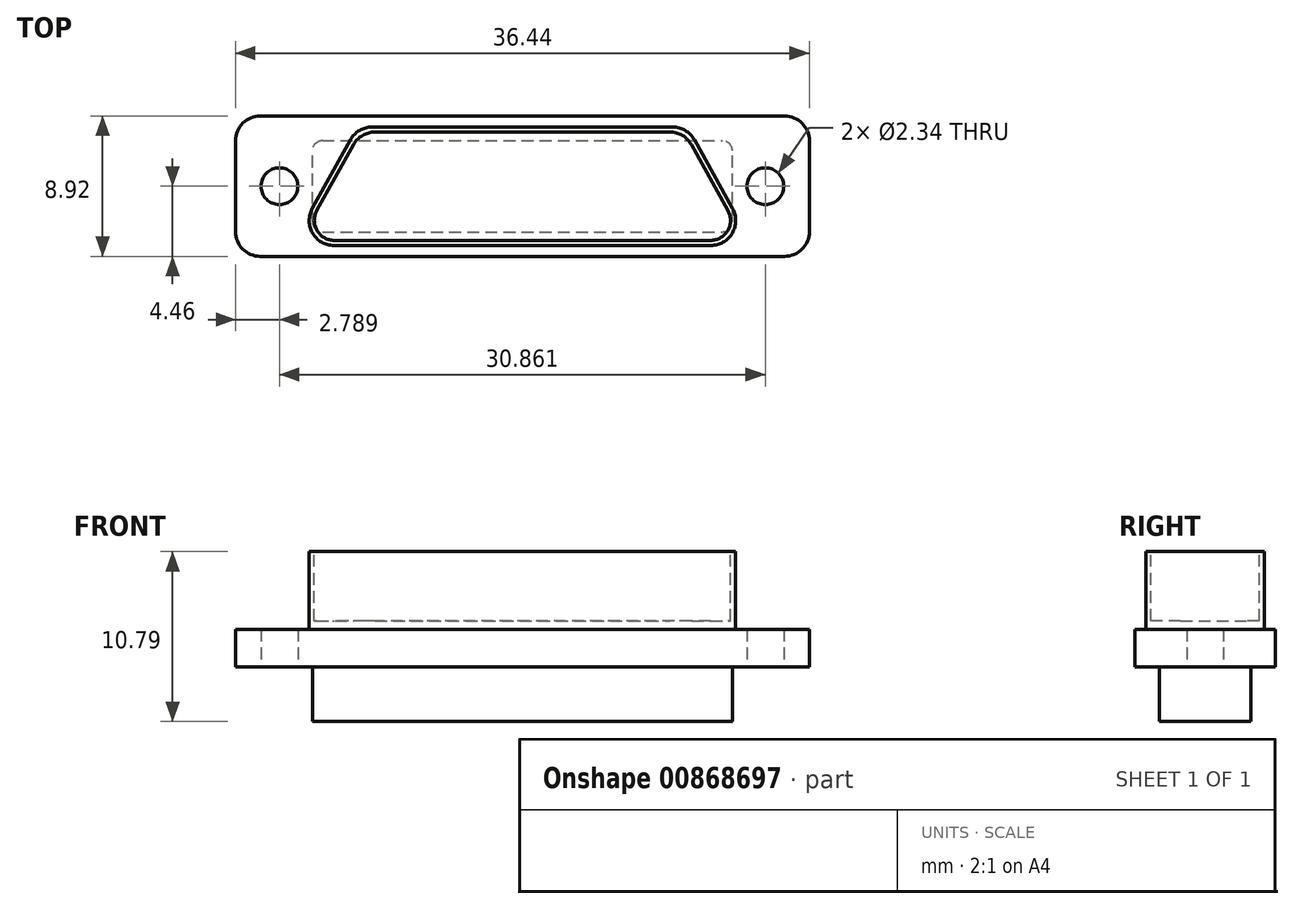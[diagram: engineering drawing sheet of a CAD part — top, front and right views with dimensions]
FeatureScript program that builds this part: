
annotation { "Feature Type Name" : "Feature", "Feature Type Description" : "" }
export const myFeature = defineFeature(function(context is Context, id is Id, definition is map)
    precondition{}
    {
        {
            var Q0;
            Q0=qCreatedBy(makeId("Top.planeOp"),FACE);
            var sketch = newSketch(context, id + "F0", { "sketchPlane" : qUnion([Q0])});
            skLineSegment(sketch, "E0.bottom", {"start": v(-16.65, 4.46) * mm, "end": v(16.65, 4.46) * mm});
            skLineSegment(sketch, "E0.top", {"start": v(-16.65, -4.46) * mm, "end": v(16.65, -4.46) * mm});
            skLineSegment(sketch, "E0.left", {"start": v(-18.22, 2.88) * mm, "end": v(-18.22, -2.88) * mm});
            skLineSegment(sketch, "E0.right", {"start": v(18.22, 2.88) * mm, "end": v(18.22, -2.88) * mm});
            skPoint(sketch, "E0.middle", {"position": v(0, 0) * mm});
            skCircle(sketch, "E1", {"center": v(-15.43, 0) * mm, "radius": 1.17 * mm});
            skCircle(sketch, "E2", {"center": v(15.43, 0) * mm, "radius": 1.17 * mm});
            skPoint(sketch, "E3.visualSharp", {"position": v(-18.22, -4.46) * mm});
            skArc(sketch, "E3.filletArc", {"start": v(-18.22, -2.88) * mm, "mid": v(-17.76, -4) * mm, "end": v(-16.65, -4.46) * mm});
            skPoint(sketch, "E4.visualSharp", {"position": v(-18.22, 4.46) * mm});
            skArc(sketch, "E4.filletArc", {"start": v(-16.65, 4.46) * mm, "mid": v(-17.76, 4) * mm, "end": v(-18.22, 2.88) * mm});
            skPoint(sketch, "E5.visualSharp", {"position": v(18.22, 4.46) * mm});
            skArc(sketch, "E5.filletArc", {"start": v(18.22, 2.88) * mm, "mid": v(17.76, 4) * mm, "end": v(16.65, 4.46) * mm});
            skPoint(sketch, "E6.visualSharp", {"position": v(18.22, -4.46) * mm});
            skArc(sketch, "E6.filletArc", {"start": v(16.65, -4.46) * mm, "mid": v(17.76, -4) * mm, "end": v(18.22, -2.88) * mm});
            skSolve(sketch);
        }
        {
            var Q0;
            Q0=makeQuery(id+"F0.imprint","IMPRINT",FACE,{"disambiguationData":[TD([[makeQuery(id+"F0.imprint","IMPRINT",EDGE,{"derivedFrom":sQuery(id+"F0.wireOp",EDGE,"E0.bottom")}),-1.0]])]});
            extrude(context, id + "F1", {"entities" : qUnion([Q0]), "endBound" : BoundingType.SYMMETRIC, "depth" : 2.36 * mm, "offsetDistance" : 25.4 * mm});
        }
        {
            var Q0;
            Q0=makeQuery(id+"F1.opExtrude","CAP_FACE",FACE,{"disambiguationData":[OSD([sQuery(id+"F0.wireOp",EDGE,"E0.bottom"),sQuery(id+"F0.wireOp",EDGE,"E0.top"),sQuery(id+"F0.wireOp",EDGE,"E0.left"),sQuery(id+"F0.wireOp",EDGE,"E0.right"),sQuery(id+"F0.wireOp",EDGE,"E1"),sQuery(id+"F0.wireOp",EDGE,"E2"),sQuery(id+"F0.wireOp",EDGE,"E3.filletArc"),sQuery(id+"F0.wireOp",EDGE,"E4.filletArc"),sQuery(id+"F0.wireOp",EDGE,"E5.filletArc"),sQuery(id+"F0.wireOp",EDGE,"E6.filletArc")])],"isStart":false});
            var sketch = newSketch(context, id + "F2", { "sketchPlane" : qUnion([Q0])});
            skPoint(sketch, "E7.middle", {"position": v(0, 0) * mm});
            skLineSegment(sketch, "E8.top", {"start": v(11.97, -3.76) * mm, "end": v(-11.97, -3.76) * mm});
            skLineSegment(sketch, "E9", {"start": v(-9.55, 3.76) * mm, "end": v(9.55, 3.76) * mm});
            skLineSegment(sketch, "E10", {"start": v(-13.35, -1.42) * mm, "end": v(-10.93, 2.95) * mm});
            skLineSegment(sketch, "E11", {"start": v(10.93, 2.95) * mm, "end": v(13.35, -1.42) * mm});
            skPoint(sketch, "E12.visualSharp", {"position": v(-10.48, 3.76) * mm});
            skArc(sketch, "E12.filletArc", {"start": v(-9.55, 3.76) * mm, "mid": v(-10.35, 3.54) * mm, "end": v(-10.93, 2.95) * mm});
            skPoint(sketch, "E13.visualSharp", {"position": v(-14.64, -3.76) * mm});
            skArc(sketch, "E13.filletArc", {"start": v(-13.35, -1.42) * mm, "mid": v(-13.33, -2.98) * mm, "end": v(-11.97, -3.76) * mm});
            skPoint(sketch, "E14.visualSharp", {"position": v(14.64, -3.76) * mm});
            skArc(sketch, "E14.filletArc", {"start": v(11.97, -3.76) * mm, "mid": v(13.33, -2.98) * mm, "end": v(13.35, -1.42) * mm});
            skPoint(sketch, "E15.visualSharp", {"position": v(10.48, 3.76) * mm});
            skArc(sketch, "E15.filletArc", {"start": v(10.93, 2.95) * mm, "mid": v(10.35, 3.54) * mm, "end": v(9.55, 3.76) * mm});
            skSolve(sketch);
        }
        {
            var Q0;
            Q0=qSketchRegion(id+"F2",true);
            extrude(context, id + "F3", {"entities" : qUnion([Q0]), "operationType" : NewBodyOperationType.ADD, "depth" : 4.95 * mm, "offsetDistance" : 25.4 * mm});
        }
        {
            var Q0;
            Q0=makeQuery(id+"F1.opExtrude","CAP_FACE",FACE,{"disambiguationData":[OSD([sQuery(id+"F0.wireOp",EDGE,"E0.bottom"),sQuery(id+"F0.wireOp",EDGE,"E0.top"),sQuery(id+"F0.wireOp",EDGE,"E0.left"),sQuery(id+"F0.wireOp",EDGE,"E0.right"),sQuery(id+"F0.wireOp",EDGE,"E1"),sQuery(id+"F0.wireOp",EDGE,"E2"),sQuery(id+"F0.wireOp",EDGE,"E3.filletArc"),sQuery(id+"F0.wireOp",EDGE,"E4.filletArc"),sQuery(id+"F0.wireOp",EDGE,"E5.filletArc"),sQuery(id+"F0.wireOp",EDGE,"E6.filletArc")])],"isStart":true});
            var sketch = newSketch(context, id + "F4", { "sketchPlane" : qUnion([Q0])});
            skLineSegment(sketch, "E16.bottom", {"start": v(-12.7, 2.9) * mm, "end": v(12.7, 2.9) * mm});
            skLineSegment(sketch, "E16.top", {"start": v(-12.7, -2.9) * mm, "end": v(12.7, -2.9) * mm});
            skLineSegment(sketch, "E16.left", {"start": v(-13.34, 2.26) * mm, "end": v(-13.34, -2.26) * mm});
            skLineSegment(sketch, "E16.right", {"start": v(13.34, 2.26) * mm, "end": v(13.34, -2.26) * mm});
            skPoint(sketch, "E16.middle", {"position": v(0, 0) * mm});
            skPoint(sketch, "E17.visualSharp", {"position": v(-13.34, 2.9) * mm});
            skArc(sketch, "E17.filletArc", {"start": v(-12.7, 2.9) * mm, "mid": v(-13.15, 2.7) * mm, "end": v(-13.34, 2.26) * mm});
            skPoint(sketch, "E18.visualSharp", {"position": v(-13.34, -2.9) * mm});
            skArc(sketch, "E18.filletArc", {"start": v(-13.34, -2.26) * mm, "mid": v(-13.15, -2.7) * mm, "end": v(-12.7, -2.9) * mm});
            skPoint(sketch, "E19.visualSharp", {"position": v(13.34, -2.9) * mm});
            skArc(sketch, "E19.filletArc", {"start": v(12.7, -2.9) * mm, "mid": v(13.15, -2.7) * mm, "end": v(13.34, -2.26) * mm});
            skPoint(sketch, "E20.visualSharp", {"position": v(13.34, 2.9) * mm});
            skArc(sketch, "E20.filletArc", {"start": v(13.34, 2.26) * mm, "mid": v(13.15, 2.7) * mm, "end": v(12.7, 2.9) * mm});
            skSolve(sketch);
        }
        {
            var Q0;
            Q0=qSketchRegion(id+"F4",true);
            extrude(context, id + "F5", {"entities" : qUnion([Q0]), "operationType" : NewBodyOperationType.ADD, "depth" : 3.48 * mm, "offsetDistance" : 25.4 * mm});
        }
        {
            var Q0;
            Q0=makeQuery(id+"F3.opExtrude","CAP_FACE",FACE,{"disambiguationData":[OSD([sQuery(id+"F2.wireOp",EDGE,"E8.top"),sQuery(id+"F2.wireOp",EDGE,"E9"),sQuery(id+"F2.wireOp",EDGE,"E10"),sQuery(id+"F2.wireOp",EDGE,"E11"),sQuery(id+"F2.wireOp",EDGE,"E12.filletArc"),sQuery(id+"F2.wireOp",EDGE,"E13.filletArc"),sQuery(id+"F2.wireOp",EDGE,"E14.filletArc"),sQuery(id+"F2.wireOp",EDGE,"E15.filletArc")])],"isStart":false});
            var sketch = newSketch(context, id + "F6", { "sketchPlane" : qUnion([Q0])});
            skLineSegment(sketch, "E21", {"start": v(-9.36, 3.44) * mm, "end": v(9.36, 3.44) * mm});
            skLineSegment(sketch, "E22", {"start": v(10.74, 2.63) * mm, "end": v(13.06, -1.56) * mm});
            skLineSegment(sketch, "E23", {"start": v(11.95, -3.44) * mm, "end": v(-11.95, -3.44) * mm});
            skLineSegment(sketch, "E24", {"start": v(-13.06, -1.56) * mm, "end": v(-10.74, 2.63) * mm});
            skPoint(sketch, "E25.visualSharp", {"position": v(-14.1, -3.44) * mm});
            skArc(sketch, "E25.filletArc", {"start": v(-13.06, -1.56) * mm, "mid": v(-13.04, -2.82) * mm, "end": v(-11.95, -3.44) * mm});
            skPoint(sketch, "E26.visualSharp", {"position": v(-10.29, 3.44) * mm});
            skArc(sketch, "E26.filletArc", {"start": v(-9.36, 3.44) * mm, "mid": v(-10.16, 3.22) * mm, "end": v(-10.74, 2.63) * mm});
            skPoint(sketch, "E27.visualSharp", {"position": v(10.3, 3.44) * mm});
            skArc(sketch, "E27.filletArc", {"start": v(10.74, 2.63) * mm, "mid": v(10.16, 3.22) * mm, "end": v(9.36, 3.44) * mm});
            skPoint(sketch, "E28.visualSharp", {"position": v(14.1, -3.44) * mm});
            skArc(sketch, "E28.filletArc", {"start": v(11.95, -3.44) * mm, "mid": v(13.04, -2.82) * mm, "end": v(13.06, -1.56) * mm});
            skSolve(sketch);
        }
        {
            var Q0;
            Q0=qSketchRegion(id+"F6",true);
            extrude(context, id + "F7", {"entities" : qUnion([Q0]), "operationType" : NewBodyOperationType.REMOVE, "depth" : -4.4 * mm, "offsetDistance" : 25.4 * mm});
        }
    });
